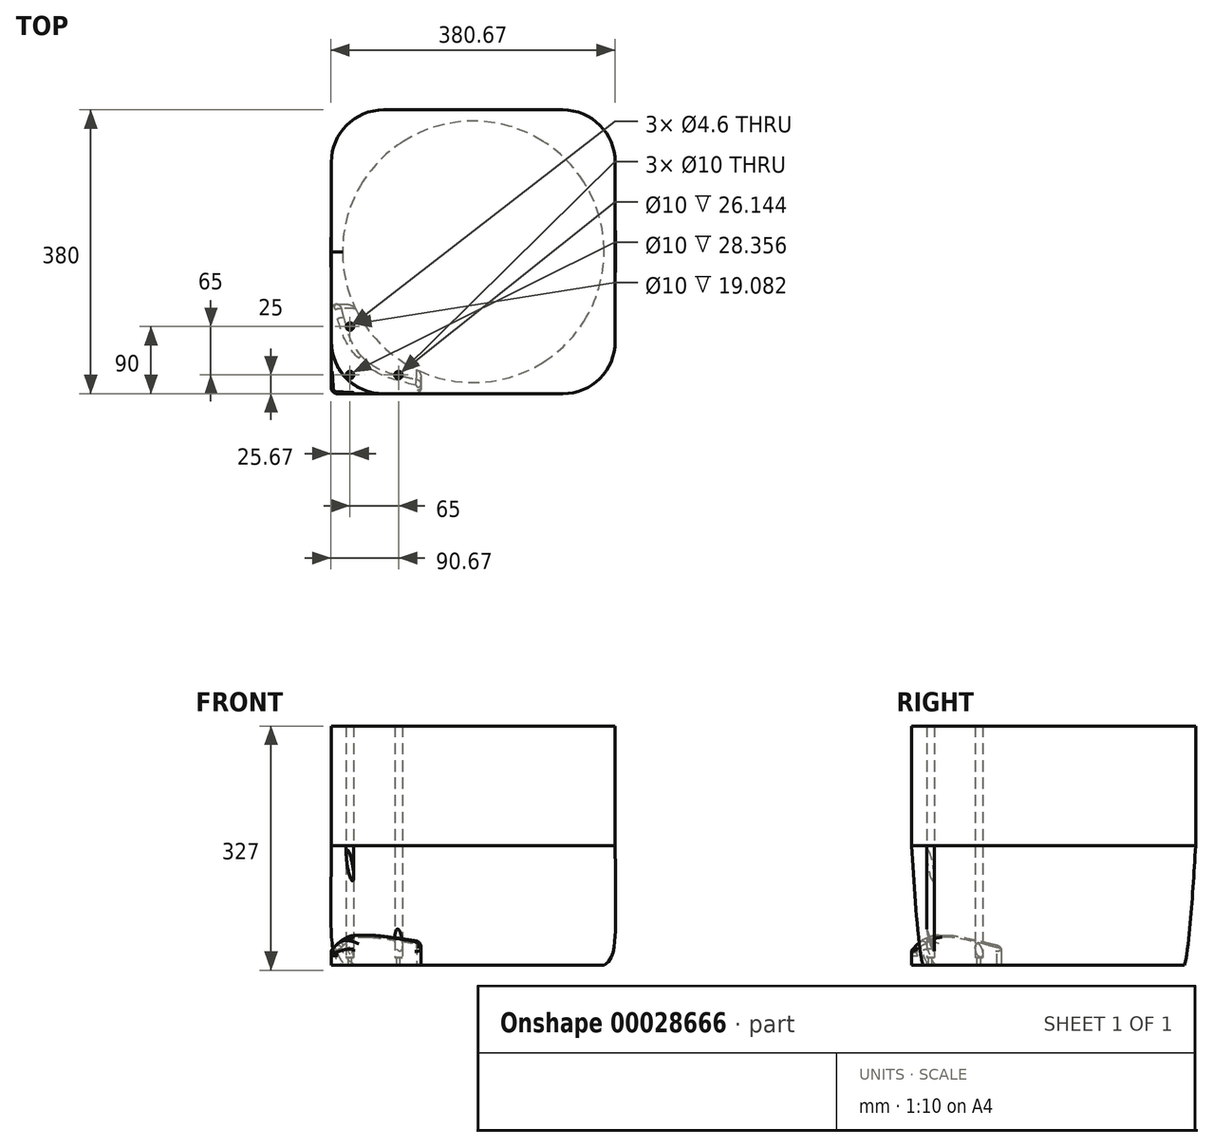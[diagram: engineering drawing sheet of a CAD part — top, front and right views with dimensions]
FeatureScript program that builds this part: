
annotation { "Feature Type Name" : "Feature", "Feature Type Description" : "" }
export const myFeature = defineFeature(function(context is Context, id is Id, definition is map)
    precondition{}
    {
        {
            var Q0;
            Q0=qCreatedBy(makeId("Top.planeOp"),FACE);
            var sketch = newSketch(context, id + "F0", { "sketchPlane" : qUnion([Q0])});
            skLineSegment(sketch, "E0.bottom", {"start": v(-190, 190) * mm, "end": v(190, 190) * mm});
            skLineSegment(sketch, "E0.top", {"start": v(-190, -190) * mm, "end": v(190, -190) * mm});
            skLineSegment(sketch, "E0.left", {"start": v(-190, 190) * mm, "end": v(-190, -190) * mm});
            skLineSegment(sketch, "E0.right", {"start": v(190, 190) * mm, "end": v(190, -190) * mm});
            skPoint(sketch, "E1", {"position": v(0, 190) * mm});
            skPoint(sketch, "E2", {"position": v(-190, 0) * mm});
            skLineSegment(sketch, "E3", {"start": v(-190, 0) * mm, "end": v(190, 0) * mm, "construction": true});
            skPoint(sketch, "E4", {"position": v(0, 0) * mm});
            skCircle(sketch, "E5", {"center": v(0, 0) * mm, "radius": 175 * mm, "construction": true});
            skSolve(sketch);
        }
        {
            var Q0;
            Q0=makeQuery(id+"F0.imprint","IMPRINT",FACE,{"disambiguationData":[TD([[makeQuery(id+"F0.imprint","IMPRINT",EDGE,{"derivedFrom":sQuery(id+"F0.wireOp",EDGE,"E0.bottom")}),-1.0]])]});
            extrude(context, id + "F1", {"entities" : qUnion([Q0]), "depth" : 160 * mm, "offsetDistance" : 25 * mm});
        }
        {
            var Q0;
            Q0=makeQuery(id+"F1.opExtrude","SWEPT_EDGE",EDGE,{"disambiguationData":[OSD([sQuery(id+"F0.wireOp",EDGE,"E0.top"),sQuery(id+"F0.wireOp",EDGE,"E0.left")])]});
            var Q1;
            Q1=makeQuery(id+"F1.opExtrude","SWEPT_EDGE",EDGE,{"disambiguationData":[OSD([sQuery(id+"F0.wireOp",EDGE,"E0.top"),sQuery(id+"F0.wireOp",EDGE,"E0.right")])]});
            var Q2;
            Q2=makeQuery(id+"F1.opExtrude","SWEPT_EDGE",EDGE,{"disambiguationData":[OSD([sQuery(id+"F0.wireOp",EDGE,"E0.bottom"),sQuery(id+"F0.wireOp",EDGE,"E0.right")])]});
            var Q3;
            Q3=makeQuery(id+"F1.opExtrude","SWEPT_EDGE",EDGE,{"disambiguationData":[OSD([sQuery(id+"F0.wireOp",EDGE,"E0.bottom"),sQuery(id+"F0.wireOp",EDGE,"E0.left")])]});
            fillet(context, id + "F2", {"entities" : qUnion([Q0, Q1, Q2, Q3]), "tangentPropagation" : true, "radius" : 70 * mm, "defaultsChanged" : true, "vertexSettings" : [], "allowEdgeOverflow" : false});
        }
        {
            var Q0;
            Q0=makeQuery(id+"F0.imprint","IMPRINT",FACE,{"disambiguationData":[TD([[makeQuery(id+"F0.imprint","IMPRINT",EDGE,{"derivedFrom":sQuery(id+"F0.wireOp",EDGE,"E0.bottom")}),-1.0]])]});
            cPlane(context, id + "F3", {"entities" : qUnion([Q0]), "cplaneType" : CPlaneType.OFFSET, "offset" : 160 * mm, "oppositeDirection" : true, "width" : 150 * mm, "height" : 150 * mm});
        }
        {
            var Q0;
            Q0=qCreatedBy(id+"F3.planeOp",FACE);
            var sketch = newSketch(context, id + "F4", { "sketchPlane" : qUnion([Q0])});
            skLineSegment(sketch, "E6", {"start": v(0, -238.41) * mm, "end": v(0, 305.1) * mm, "construction": true});
            skLineSegment(sketch, "E7", {"start": v(-284.91, 0) * mm, "end": v(337.5, 0) * mm, "construction": true});
            skLineSegment(sketch, "E8", {"start": v(-130.04, -205.9) * mm, "end": v(-93.45, -147.96) * mm, "construction": true});
            skLineSegment(sketch, "E9.MirrorCS", {"start": v(130.04, -205.9) * mm, "end": v(-148.6, 235.27) * mm, "construction": true});
            skLineSegment(sketch, "E10", {"start": v(262.97, -262.97) * mm, "end": v(-306.9, 306.9) * mm, "construction": true});
            skLineSegment(sketch, "E11.MirrorCS", {"start": v(205.9, -130.04) * mm, "end": v(-235.27, 148.6) * mm, "construction": true});
            skLineSegment(sketch, "E12.MirrorCS", {"start": v(205.9, 130.04) * mm, "end": v(147.96, 93.45) * mm, "construction": true});
            skLineSegment(sketch, "E13", {"start": v(-93.45, -147.96) * mm, "end": v(148.6, 235.27) * mm, "construction": true});
            skLineSegment(sketch, "E14", {"start": v(147.96, 93.45) * mm, "end": v(-235.27, -148.6) * mm, "construction": true});
            skArc(sketch, "E15", {"start": v(147.96, 93.45) * mm, "mid": v(123.74, 123.74) * mm, "end": v(93.45, 147.96) * mm});
            skArc(sketch, "E16", {"start": v(93.45, 147.96) * mm, "mid": v(0, 175) * mm, "end": v(-93.45, 147.96) * mm});
            skArc(sketch, "E17.MirrorCS", {"start": v(-147.96, 93.45) * mm, "mid": v(-123.74, 123.74) * mm, "end": v(-93.45, 147.96) * mm});
            skArc(sketch, "E18.MirrorCS", {"start": v(-147.96, -93.45) * mm, "mid": v(-175, 0) * mm, "end": v(-147.96, 93.45) * mm});
            skArc(sketch, "E19.MirrorCS", {"start": v(-147.96, -93.45) * mm, "mid": v(-123.74, -123.74) * mm, "end": v(-93.45, -147.96) * mm});
            skArc(sketch, "E20", {"start": v(147.96, -93.45) * mm, "mid": v(123.74, -123.74) * mm, "end": v(93.45, -147.96) * mm});
            skArc(sketch, "E21.MirrorCS", {"start": v(93.45, -147.96) * mm, "mid": v(0, -175) * mm, "end": v(-93.45, -147.96) * mm});
            skArc(sketch, "E22.MirrorCS", {"start": v(147.96, -93.45) * mm, "mid": v(175, 0) * mm, "end": v(147.96, 93.45) * mm});
            skSolve(sketch);
        }
        {
            var Q0;
            Q0=qCreatedBy(makeId("Front.planeOp"),FACE);
            var sketch = newSketch(context, id + "F5", { "sketchPlane" : qUnion([Q0])});
            skFitSpline(sketch, "E23", {"points": [v(-190, 0) * mm, v(-188.88, -131.47) * mm, v(-175, -160) * mm], "startDerivative": vector(-0.12, -252.4) * mm, "endDerivative": vector(86.29, -52.4) * mm});
            skLineSegment(sketch, "E24", {"start": v(0, 195.1) * mm, "end": v(0, -184.2) * mm, "construction": true});
            skLineSegment(sketch, "E25", {"start": v(0, -184.2) * mm, "end": v(-1.47, -184.2) * mm, "construction": true});
            skFitSpline(sketch, "E26.MirrorCS", {"points": [v(190, 0) * mm, v(188.88, -131.47) * mm, v(175, -160) * mm], "startDerivative": vector(0.12, -252.4) * mm, "endDerivative": vector(-86.29, -52.4) * mm});
            skLineSegment(sketch, "E27", {"start": v(-189.99, 187.2) * mm, "end": v(-192.57, -182.37) * mm, "construction": true});
            skSolve(sketch);
        }
        {
            var Q0;
            Q0=makeQuery(id+"F1.opExtrude","CAP_FACE",FACE,{"disambiguationData":[OSD([sQuery(id+"F0.wireOp",EDGE,"E0.bottom"),sQuery(id+"F0.wireOp",EDGE,"E0.top"),sQuery(id+"F0.wireOp",EDGE,"E0.left"),sQuery(id+"F0.wireOp",EDGE,"E0.right")])],"isStart":true});
            var Q1;
            Q1=makeQuery(id+"F4.imprint","IMPRINT",FACE,{"disambiguationData":[TD([[makeQuery(id+"F4.imprint","IMPRINT",EDGE,{"derivedFrom":sQuery(id+"F4.wireOp",EDGE,"E15")}),1.0]])]});
            var Q2;
            Q2=sQuery(id+"F5.wireOp",EDGE,"E23");
            var Q3;
            Q3=sQuery(id+"F5.wireOp",EDGE,"E26.MirrorCS");
            var Q4;
            Q4=sQuery(id+"F5.wireOp",EDGE,"d5981630-7dc7-4bfb-b74d-dd79564826400.MirrorCS");
            var Q5;
            Q5=sQuery(id+"F5.wireOp",EDGE,"e7aa1f66-91db-406d-b71e-a97bfbe85a65");
            loft(context, id + "F6", {"operationType" : NewBodyOperationType.ADD, "sheetProfilesArray" : [{ "sheetProfileEntities" : qUnion([Q0]) }, { "sheetProfileEntities" : qUnion([Q1]) }], "addGuides" : true, "guidesArray" : [{ "guideEntities" : qUnion([Q2]), "guideDerivativeType" : LoftGuideDerivativeType.DEFAULT, "guideDerivativeMagnitude" : 1 }, { "guideEntities" : qUnion([Q3]), "guideDerivativeType" : LoftGuideDerivativeType.DEFAULT, "guideDerivativeMagnitude" : 1 }], "spine" : qUnion([Q4, Q5])});
        }
        {
            var Q0;
            Q0=qCreatedBy(id+"F3.planeOp",FACE);
            var sketch = newSketch(context, id + "F7", { "sketchPlane" : qUnion([Q0])});
            skLineSegment(sketch, "E28.bottom", {"start": v(-190, -190) * mm, "end": v(-70, -190) * mm});
            skLineSegment(sketch, "E28.top", {"start": v(-190, -70) * mm, "end": v(-70, -70) * mm});
            skLineSegment(sketch, "E28.left", {"start": v(-190, -190) * mm, "end": v(-190, -70) * mm});
            skLineSegment(sketch, "E28.right", {"start": v(-70, -190) * mm, "end": v(-70, -70) * mm});
            skSolve(sketch);
        }
        {
            var Q0;
            Q0 = qSketchRegion(id + "F7", true);
            extrude(context, id + "F8", {"entities" : qUnion([Q0]), "depth" : 40 * mm, "offsetDistance" : 25 * mm});
        }
        {
            var Q0;
            Q0=makeQuery(id+"F1.opExtrude","SWEPT_BODY",BODY,{"disambiguationData":[OSD([sQuery(id+"F0.wireOp",EDGE,"E0.bottom"),sQuery(id+"F0.wireOp",EDGE,"E0.top"),sQuery(id+"F0.wireOp",EDGE,"E0.left"),sQuery(id+"F0.wireOp",EDGE,"E0.right")])]});
            var Q1;
            Q1=makeQuery(id+"F8.opExtrude","SWEPT_BODY",BODY,{"disambiguationData":[OSD([sQuery(id+"F7.wireOp",EDGE,"E28.bottom"),sQuery(id+"F7.wireOp",EDGE,"E28.top"),sQuery(id+"F7.wireOp",EDGE,"E28.left"),sQuery(id+"F7.wireOp",EDGE,"E28.right")])]});
            booleanBodies(context, id + "F9", {"operationType" : BooleanOperationType.SUBTRACTION, "tools" : qUnion([Q0]), "targets" : qUnion([Q1]), "keepTools" : true});
        }
        {
            var Q0;
            Q0=makeQuery(id+"F8.opExtrude","CAP_EDGE",EDGE,{"disambiguationData":[OSD([sQuery(id+"F7.wireOp",EDGE,"E28.bottom")])],"isStart":false});
            var Q1;
            Q1=makeQuery(id+"F8.opExtrude","CAP_EDGE",EDGE,{"disambiguationData":[OSD([sQuery(id+"F7.wireOp",EDGE,"E28.left")])],"isStart":false});
            chamfer(context, id + "F10", {"entities" : qUnion([Q0, Q1]), "width" : 20 * mm, "tangentPropagation" : true});
        }
        {
            var Q0;
            Q0=makeQuery(id+"F9.opBoolean","INTERSECT",EDGE,{"derivedFrom":[makeQuery(id+"F6.opLoft","SWEPT_FACE",FACE,{"disambiguationData":[OSD([sQuery(id+"F0.wireOp",EDGE,"E0.bottom"),sQuery(id+"F0.wireOp",EDGE,"E0.top"),sQuery(id+"F0.wireOp",EDGE,"E0.left"),sQuery(id+"F0.wireOp",EDGE,"E0.right"),sQuery(id+"F4.wireOp",EDGE,"E15"),sQuery(id+"F4.wireOp",EDGE,"E16"),sQuery(id+"F4.wireOp",EDGE,"E17.MirrorCS"),sQuery(id+"F4.wireOp",EDGE,"E18.MirrorCS"),sQuery(id+"F4.wireOp",EDGE,"E19.MirrorCS"),sQuery(id+"F4.wireOp",EDGE,"E20"),sQuery(id+"F4.wireOp",EDGE,"E21.MirrorCS"),sQuery(id+"F4.wireOp",EDGE,"E22.MirrorCS"),sQuery(id+"F5.wireOp",VERTEX,"E23.start"),sQuery(id+"F5.wireOp",VERTEX,"E23.end"),sQuery(id+"F5.wireOp",VERTEX,"E26.MirrorCS.start"),sQuery(id+"F5.wireOp",VERTEX,"E26.MirrorCS.end"),sQuery(id+"F5.wireOp",EDGE,"E23"),sQuery(id+"F5.wireOp",EDGE,"E26.MirrorCS")])]}),makeQuery(id+"F8.opExtrude","SWEPT_FACE",FACE,{"disambiguationData":[OSD([sQuery(id+"F7.wireOp",EDGE,"E28.right")])]})]});
            var Q1;
            Q1=makeQuery(id+"F8.opExtrude","SWEPT_EDGE",EDGE,{"disambiguationData":[OSD([sQuery(id+"F7.wireOp",EDGE,"E28.bottom"),sQuery(id+"F7.wireOp",EDGE,"E28.right")])]});
            var Q2;
            Q2=makeQuery(id+"F8.opExtrude","SWEPT_EDGE",EDGE,{"disambiguationData":[OSD([sQuery(id+"F7.wireOp",EDGE,"E28.bottom"),sQuery(id+"F7.wireOp",EDGE,"E28.left")])]});
            var Q3;
            Q3=makeQuery(id+"F8.opExtrude","SWEPT_EDGE",EDGE,{"disambiguationData":[OSD([sQuery(id+"F7.wireOp",EDGE,"E28.top"),sQuery(id+"F7.wireOp",EDGE,"E28.left")])]});
            var Q4;
            Q4=makeQuery(id+"F9.opBoolean","INTERSECT",EDGE,{"derivedFrom":[makeQuery(id+"F6.opLoft","SWEPT_FACE",FACE,{"disambiguationData":[OSD([sQuery(id+"F0.wireOp",EDGE,"E0.bottom"),sQuery(id+"F0.wireOp",EDGE,"E0.top"),sQuery(id+"F0.wireOp",EDGE,"E0.left"),sQuery(id+"F0.wireOp",EDGE,"E0.right"),sQuery(id+"F4.wireOp",EDGE,"E15"),sQuery(id+"F4.wireOp",EDGE,"E16"),sQuery(id+"F4.wireOp",EDGE,"E17.MirrorCS"),sQuery(id+"F4.wireOp",EDGE,"E18.MirrorCS"),sQuery(id+"F4.wireOp",EDGE,"E19.MirrorCS"),sQuery(id+"F4.wireOp",EDGE,"E20"),sQuery(id+"F4.wireOp",EDGE,"E21.MirrorCS"),sQuery(id+"F4.wireOp",EDGE,"E22.MirrorCS"),sQuery(id+"F5.wireOp",VERTEX,"E23.start"),sQuery(id+"F5.wireOp",VERTEX,"E23.end"),sQuery(id+"F5.wireOp",VERTEX,"E26.MirrorCS.start"),sQuery(id+"F5.wireOp",VERTEX,"E26.MirrorCS.end"),sQuery(id+"F5.wireOp",EDGE,"E23"),sQuery(id+"F5.wireOp",EDGE,"E26.MirrorCS")])]}),makeQuery(id+"F8.opExtrude","SWEPT_FACE",FACE,{"disambiguationData":[OSD([sQuery(id+"F7.wireOp",EDGE,"E28.top")])]})]});
            fillet(context, id + "F11", {"entities" : qUnion([Q0, Q1, Q2, Q3, Q4]), "tangentPropagation" : true, "radius" : 8 * mm, "defaultsChanged" : true, "vertexSettings" : [], "allowEdgeOverflow" : false});
        }
        {
            var Q0;
            Q0=makeQuery(id+"F10.opChamfer","BLEND_EDGE",EDGE,{"blendedFrom":[makeQuery(id+"F8.opExtrude","CAP_EDGE",EDGE,{"disambiguationData":[OSD([sQuery(id+"F7.wireOp",EDGE,"E28.bottom")])],"isStart":false}),makeQuery(id+"F8.opExtrude","CAP_EDGE",EDGE,{"disambiguationData":[OSD([sQuery(id+"F7.wireOp",EDGE,"E28.left")])],"isStart":false})],"blendedInto":[]});
            fillet(context, id + "F12", {"entities" : qUnion([Q0]), "tangentPropagation" : true, "radius" : 40 * mm, "defaultsChanged" : true, "vertexSettings" : [], "allowEdgeOverflow" : false});
        }
        {
            var Q0;
            {var subQ0=sQuery(id+"F7.wireOp",EDGE,"E28.bottom");Q0=makeQuery(id+"F10.opChamfer","BLEND_EDGE",EDGE,{"blendedFrom":[makeQuery(id+"F8.opExtrude","CAP_EDGE",EDGE,{"disambiguationData":[OSD([subQ0])],"isStart":false}),makeQuery(id+"F8.opExtrude","CAP_FACE",FACE,{"disambiguationData":[OSD([subQ0,sQuery(id+"F7.wireOp",EDGE,"E28.top"),sQuery(id+"F7.wireOp",EDGE,"E28.left"),sQuery(id+"F7.wireOp",EDGE,"E28.right")])],"isStart":false})],"blendedInto":[makeQuery(id+"F8.opExtrude","CAP_FACE",FACE,{"disambiguationData":[OSD([subQ0,sQuery(id+"F7.wireOp",EDGE,"E28.top"),sQuery(id+"F7.wireOp",EDGE,"E28.left"),sQuery(id+"F7.wireOp",EDGE,"E28.right")])],"isStart":false})]});}
            var Q1;
            {var subQ0=sQuery(id+"F7.wireOp",EDGE,"E28.left");Q1=makeQuery(id+"F10.opChamfer","BLEND_EDGE",EDGE,{"blendedFrom":[makeQuery(id+"F8.opExtrude","CAP_EDGE",EDGE,{"disambiguationData":[OSD([subQ0])],"isStart":false}),makeQuery(id+"F8.opExtrude","CAP_FACE",FACE,{"disambiguationData":[OSD([sQuery(id+"F7.wireOp",EDGE,"E28.bottom"),sQuery(id+"F7.wireOp",EDGE,"E28.top"),subQ0,sQuery(id+"F7.wireOp",EDGE,"E28.right")])],"isStart":false})],"blendedInto":[makeQuery(id+"F8.opExtrude","CAP_FACE",FACE,{"disambiguationData":[OSD([sQuery(id+"F7.wireOp",EDGE,"E28.bottom"),sQuery(id+"F7.wireOp",EDGE,"E28.top"),subQ0,sQuery(id+"F7.wireOp",EDGE,"E28.right")])],"isStart":false})]});}
            fillet(context, id + "F13", {"entities" : qUnion([Q0, Q1]), "tangentPropagation" : true, "radius" : 40 * mm, "defaultsChanged" : true, "vertexSettings" : [], "allowEdgeOverflow" : false});
        }
        {
            var Q0;
            Q0=makeQuery(id+"F9.opBoolean","INTERSECT",EDGE,{"derivedFrom":[makeQuery(id+"F6.opLoft","SWEPT_FACE",FACE,{"disambiguationData":[OSD([sQuery(id+"F0.wireOp",EDGE,"E0.bottom"),sQuery(id+"F0.wireOp",EDGE,"E0.top"),sQuery(id+"F0.wireOp",EDGE,"E0.left"),sQuery(id+"F0.wireOp",EDGE,"E0.right"),sQuery(id+"F4.wireOp",EDGE,"E15"),sQuery(id+"F4.wireOp",EDGE,"E16"),sQuery(id+"F4.wireOp",EDGE,"E17.MirrorCS"),sQuery(id+"F4.wireOp",EDGE,"E18.MirrorCS"),sQuery(id+"F4.wireOp",EDGE,"E19.MirrorCS"),sQuery(id+"F4.wireOp",EDGE,"E20"),sQuery(id+"F4.wireOp",EDGE,"E21.MirrorCS"),sQuery(id+"F4.wireOp",EDGE,"E22.MirrorCS"),sQuery(id+"F5.wireOp",VERTEX,"E23.start"),sQuery(id+"F5.wireOp",VERTEX,"E23.end"),sQuery(id+"F5.wireOp",VERTEX,"E26.MirrorCS.start"),sQuery(id+"F5.wireOp",VERTEX,"E26.MirrorCS.end"),sQuery(id+"F5.wireOp",EDGE,"E23"),sQuery(id+"F5.wireOp",EDGE,"E26.MirrorCS")])]}),makeQuery(id+"F8.opExtrude","CAP_FACE",FACE,{"disambiguationData":[OSD([sQuery(id+"F7.wireOp",EDGE,"E28.bottom"),sQuery(id+"F7.wireOp",EDGE,"E28.top"),sQuery(id+"F7.wireOp",EDGE,"E28.left"),sQuery(id+"F7.wireOp",EDGE,"E28.right")])],"isStart":false})]});
            fillet(context, id + "F14", {"entities" : qUnion([Q0]), "tangentPropagation" : true, "radius" : 5 * mm, "defaultsChanged" : true, "vertexSettings" : [], "allowEdgeOverflow" : false});
        }
        {
            var Q0;
            Q0=qCreatedBy(id+"F3.planeOp",FACE);
            cPlane(context, id + "F15", {"entities" : qUnion([Q0]), "cplaneType" : CPlaneType.OFFSET, "offset" : 10 * mm, "width" : 150 * mm, "height" : 150 * mm});
        }
        {
            var Q0;
            Q0=qCreatedBy(id+"F15.planeOp",FACE);
            var sketch = newSketch(context, id + "F16", { "sketchPlane" : qUnion([Q0])});
            skCircle(sketch, "E29", {"center": v(-165, -165) * mm, "radius": 5 * mm});
            skCircle(sketch, "E30", {"center": v(-100, -165) * mm, "radius": 5 * mm});
            skLineSegment(sketch, "E31", {"start": v(-278.88, -278.88) * mm, "end": v(74.08, 74.08) * mm, "construction": true});
            skLineSegment(sketch, "E32", {"start": v(-192.63, -165) * mm, "end": v(60.31, -165) * mm, "construction": true});
            skCircle(sketch, "E33.MirrorC", {"center": v(-165, -100) * mm, "radius": 5 * mm});
            skSolve(sketch);
        }
        {
            var Q0;
            Q0 = qSketchRegion(id + "F16", true);
            extrude(context, id + "F17", {"entities" : qUnion([Q0]), "operationType" : NewBodyOperationType.REMOVE, "endBound" : BoundingType.THROUGH_ALL, "depth" : 25 * mm, "offsetDistance" : 25 * mm});
        }
        {
            var Q0;
            Q0=qCreatedBy(id+"F15.planeOp",FACE);
            var sketch = newSketch(context, id + "F18", { "sketchPlane" : qUnion([Q0])});
            skCircle(sketch, "E34", {"center": v(-165, -100) * mm, "radius": 2.3 * mm});
            skCircle(sketch, "E35", {"center": v(-165, -165) * mm, "radius": 2.3 * mm});
            skCircle(sketch, "E36", {"center": v(-100, -165) * mm, "radius": 2.3 * mm});
            skSolve(sketch);
        }
        {
            var Q0;
            Q0 = qSketchRegion(id + "F18", true);
            extrude(context, id + "F19", {"entities" : qUnion([Q0]), "operationType" : NewBodyOperationType.REMOVE, "endBound" : BoundingType.THROUGH_ALL, "oppositeDirection" : true, "depth" : 25 * mm, "offsetDistance" : 25 * mm});
        }
    });
